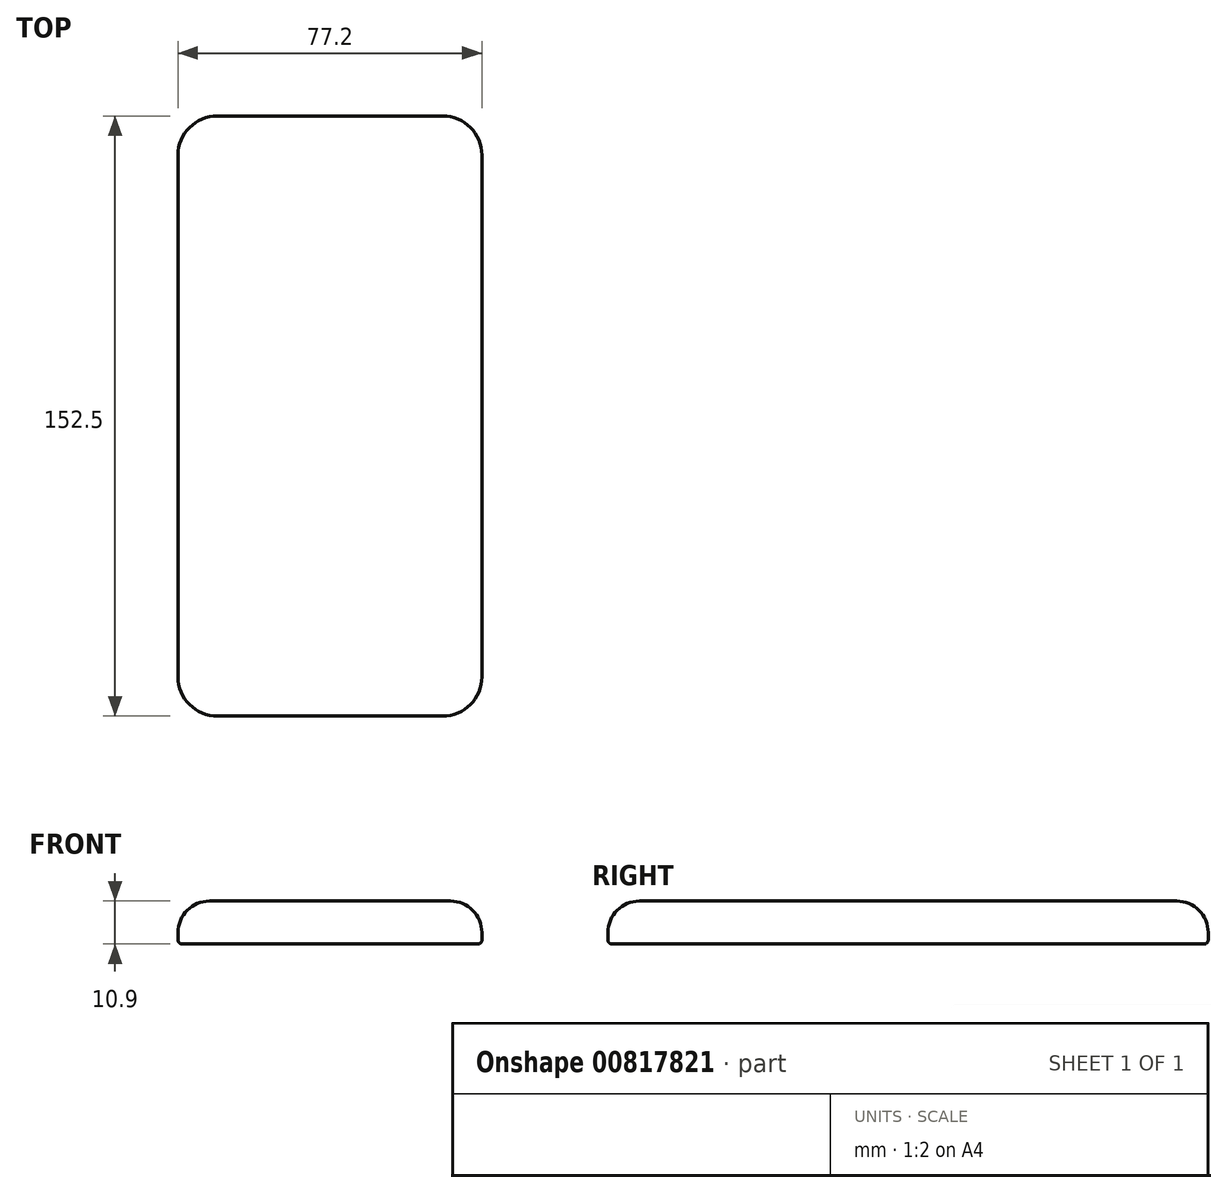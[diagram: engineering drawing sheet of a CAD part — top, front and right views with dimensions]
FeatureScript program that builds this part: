
annotation { "Feature Type Name" : "Feature", "Feature Type Description" : "" }
export const myFeature = defineFeature(function(context is Context, id is Id, definition is map)
    precondition{}
    {
        {
            var Q0;
            Q0=qCreatedBy(makeId("Top.planeOp"),FACE);
            var sketch = newSketch(context, id + "F0", { "sketchPlane" : qUnion([Q0])});
            skLineSegment(sketch, "E0.bottom", {"start": v(38.6, -76.25) * mm, "end": v(-38.6, -76.25) * mm});
            skLineSegment(sketch, "E0.top", {"start": v(38.6, 76.25) * mm, "end": v(-38.6, 76.25) * mm});
            skLineSegment(sketch, "E0.left", {"start": v(38.6, -76.25) * mm, "end": v(38.6, 76.25) * mm});
            skLineSegment(sketch, "E0.right", {"start": v(-38.6, -76.25) * mm, "end": v(-38.6, 76.25) * mm});
            skPoint(sketch, "E0.middle", {"position": v(0, 0) * mm});
            skSolve(sketch);
        }
        {
            var Q0;
            Q0=qSketchRegion(id+"F0",true);
            extrude(context, id + "F1", {"entities" : qUnion([Q0]), "depth" : 10.9 * mm, "offsetDistance" : 25 * mm});
        }
        {
            var Q0;
            Q0=makeQuery(id+"F1.opExtrude","SWEPT_EDGE",EDGE,{"disambiguationData":[OSD([sQuery(id+"F0.wireOp",EDGE,"E0.top"),sQuery(id+"F0.wireOp",EDGE,"E0.left")])]});
            var Q1;
            Q1=makeQuery(id+"F1.opExtrude","SWEPT_EDGE",EDGE,{"disambiguationData":[OSD([sQuery(id+"F0.wireOp",EDGE,"E0.top"),sQuery(id+"F0.wireOp",EDGE,"E0.right")])]});
            var Q2;
            Q2=makeQuery(id+"F1.opExtrude","SWEPT_EDGE",EDGE,{"disambiguationData":[OSD([sQuery(id+"F0.wireOp",EDGE,"E0.bottom"),sQuery(id+"F0.wireOp",EDGE,"E0.right")])]});
            var Q3;
            Q3=makeQuery(id+"F1.opExtrude","SWEPT_EDGE",EDGE,{"disambiguationData":[OSD([sQuery(id+"F0.wireOp",EDGE,"E0.bottom"),sQuery(id+"F0.wireOp",EDGE,"E0.left")])]});
            fillet(context, id + "F2", {"entities" : qUnion([Q0, Q1, Q2, Q3]), "radius" : 10 * mm, "tangentPropagation" : true, "allowEdgeOverflow" : false});
        }
        {
            var Q0;
            Q0=makeQuery(id+"F1.opExtrude","CAP_FACE",FACE,{"disambiguationData":[OSD([sQuery(id+"F0.wireOp",EDGE,"E0.bottom"),sQuery(id+"F0.wireOp",EDGE,"E0.top"),sQuery(id+"F0.wireOp",EDGE,"E0.left"),sQuery(id+"F0.wireOp",EDGE,"E0.right")])],"isStart":false});
            fillet(context, id + "F3", {"entities" : qUnion([Q0]), "radius" : 8 * mm, "tangentPropagation" : true, "allowEdgeOverflow" : false});
        }
        {
            var Q0;
            Q0=makeQuery(id+"F1.opExtrude","CAP_FACE",FACE,{"disambiguationData":[OSD([sQuery(id+"F0.wireOp",EDGE,"E0.bottom"),sQuery(id+"F0.wireOp",EDGE,"E0.top"),sQuery(id+"F0.wireOp",EDGE,"E0.left"),sQuery(id+"F0.wireOp",EDGE,"E0.right")])],"isStart":true});
            fillet(context, id + "F4", {"entities" : qUnion([Q0]), "radius" : 1 * mm, "tangentPropagation" : true, "allowEdgeOverflow" : false});
        }
    });
